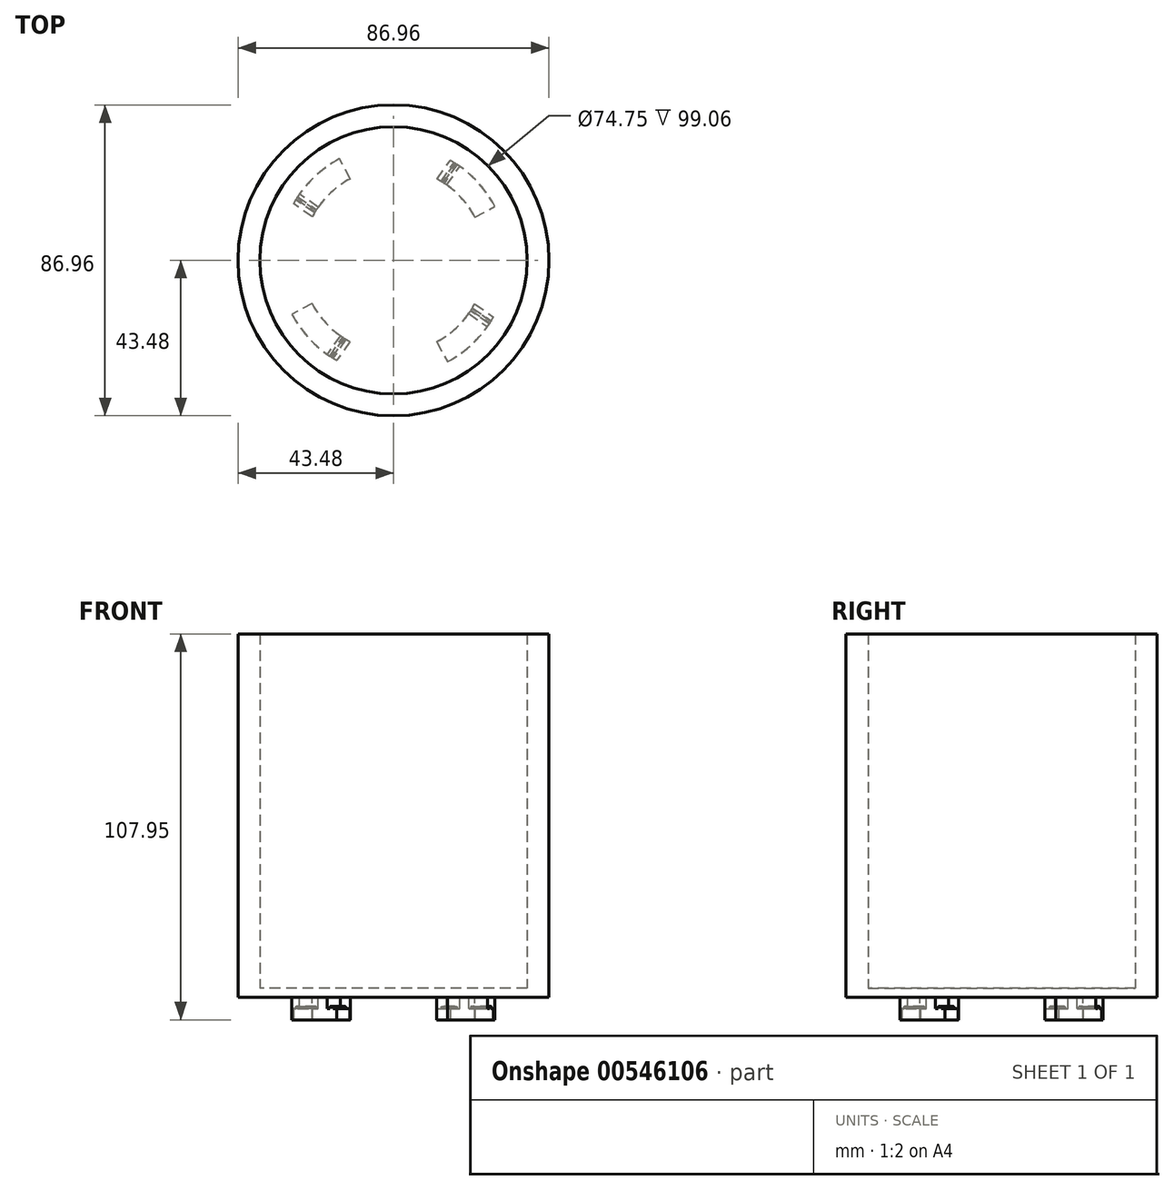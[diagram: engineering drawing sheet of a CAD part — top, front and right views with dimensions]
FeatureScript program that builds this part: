
annotation { "Feature Type Name" : "Feature", "Feature Type Description" : "" }
export const myFeature = defineFeature(function(context is Context, id is Id, definition is map)
    precondition{}
    {
        {
            var Q0;
            Q0=qCreatedBy(makeId("Top.planeOp"),FACE);
            var sketch = newSketch(context, id + "F0", { "sketchPlane" : qUnion([Q0])});
            skCircle(sketch, "E0", {"center": v(0, 0) * mm, "radius": 37.37 * mm});
            skCircle(sketch, "E1", {"center": v(0, 0) * mm, "radius": 43.48 * mm});
            skSolve(sketch);
        }
        {
            var Q0;
            Q0 = qSketchRegion(id + "F0", true);
            extrude(context, id + "F1", {"entities" : qUnion([Q0]), "depth" : 101.6 * mm, "offsetDistance" : 25.4 * mm});
        }
        {
            var Q0;
            Q0=qCreatedBy(makeId("Top.planeOp"),FACE);
            var sketch = newSketch(context, id + "F2", { "sketchPlane" : qUnion([Q0])});
            skCircle(sketch, "E2", {"center": v(0, 0) * mm, "radius": 43.48 * mm});
            skSolve(sketch);
        }
        {
            var Q0;
            Q0 = qSketchRegion(id + "F2", true);
            extrude(context, id + "F3", {"entities" : qUnion([Q0]), "operationType" : NewBodyOperationType.ADD, "depth" : 2.54 * mm, "offsetDistance" : 25.4 * mm});
        }
        {
            var Q0;
            Q0=makeQuery(id+"F3.boolean.opBoolean","MERGE",FACE,{"derivedFrom":[makeQuery(id+"F1.opExtrude","CAP_FACE",FACE,{"disambiguationData":[OSD([sQuery(id+"F0.wireOp",EDGE,"E0"),sQuery(id+"F0.wireOp",EDGE,"E1")])],"isStart":true}),makeQuery(id+"F3.opExtrude","CAP_FACE",FACE,{"disambiguationData":[OSD([sQuery(id+"F2.wireOp",EDGE,"E2")])],"isStart":true})]});
            var sketch = newSketch(context, id + "F4", { "sketchPlane" : qUnion([Q0])});
            skArc(sketch, "E3", {"start": v(15.08, 28.39) * mm, "mid": v(21.25, 24.12) * mm, "end": v(26.26, 18.53) * mm});
            skArc(sketch, "E4.0", {"start": v(12.1, 22.78) * mm, "mid": v(17.05, 19.35) * mm, "end": v(21.08, 14.87) * mm});
            skLineSegment(sketch, "E5", {"start": v(21.08, 14.87) * mm, "end": v(26.26, 18.53) * mm});
            skLineSegment(sketch, "E6", {"start": v(12.1, 22.78) * mm, "end": v(15.08, 28.39) * mm});
            skArc(sketch, "E7.1.0", {"start": v(-22.78, 12.1) * mm, "mid": v(-19.35, 17.05) * mm, "end": v(-14.87, 21.08) * mm});
            skLineSegment(sketch, "E7.1.1", {"start": v(-22.78, 12.1) * mm, "end": v(-28.39, 15.08) * mm});
            skArc(sketch, "E7.1.2", {"start": v(-28.39, 15.08) * mm, "mid": v(-24.12, 21.25) * mm, "end": v(-18.53, 26.26) * mm});
            skLineSegment(sketch, "E7.1.3", {"start": v(-14.87, 21.08) * mm, "end": v(-18.53, 26.26) * mm});
            skArc(sketch, "E7.2.0", {"start": v(-12.1, -22.78) * mm, "mid": v(-17.05, -19.35) * mm, "end": v(-21.08, -14.87) * mm});
            skLineSegment(sketch, "E7.2.1", {"start": v(-12.1, -22.78) * mm, "end": v(-15.08, -28.39) * mm});
            skArc(sketch, "E7.2.2", {"start": v(-15.08, -28.39) * mm, "mid": v(-21.25, -24.12) * mm, "end": v(-26.26, -18.53) * mm});
            skLineSegment(sketch, "E7.2.3", {"start": v(-21.08, -14.87) * mm, "end": v(-26.26, -18.53) * mm});
            skArc(sketch, "E7.3.0", {"start": v(22.78, -12.1) * mm, "mid": v(19.35, -17.05) * mm, "end": v(14.87, -21.08) * mm});
            skLineSegment(sketch, "E7.3.1", {"start": v(22.78, -12.1) * mm, "end": v(28.39, -15.08) * mm});
            skArc(sketch, "E7.3.2", {"start": v(28.39, -15.08) * mm, "mid": v(24.12, -21.25) * mm, "end": v(18.53, -26.26) * mm});
            skLineSegment(sketch, "E7.3.3", {"start": v(14.87, -21.08) * mm, "end": v(18.53, -26.26) * mm});
            skSolve(sketch);
        }
        {
            var Q0;
            Q0 = qSketchRegion(id + "F4", true);
            extrude(context, id + "F5", {"entities" : qUnion([Q0]), "operationType" : NewBodyOperationType.ADD, "depth" : 6.35 * mm, "offsetDistance" : 25.4 * mm});
        }
        {
            var Q0;
            Q0=makeQuery(id+"F5.opExtrude","CAP_FACE",FACE,{"disambiguationData":[OSD([sQuery(id+"F4.wireOp",EDGE,"E3"),sQuery(id+"F4.wireOp",EDGE,"E4.0"),sQuery(id+"F4.wireOp",EDGE,"E5"),sQuery(id+"F4.wireOp",EDGE,"E6")])],"isStart":false});
            var sketch = newSketch(context, id + "F6", { "sketchPlane" : qUnion([Q0])});
            skLineSegment(sketch, "E8.0", {"start": v(12.1, 22.78) * mm, "end": v(15.08, 28.39) * mm});
            skArc(sketch, "E8.1", {"start": v(15.08, 28.39) * mm, "mid": v(22.42, 23.04) * mm, "end": v(27.97, 15.84) * mm});
            skArc(sketch, "E8.2", {"start": v(12.1, 22.78) * mm, "mid": v(18.21, 18.26) * mm, "end": v(22.75, 12.16) * mm});
            skPoint(sketch, "E9.orphan", {"position": v(26.26, 18.53) * mm});
            skPoint(sketch, "E10.orphan", {"position": v(21.08, 14.87) * mm});
            skLineSegment(sketch, "E11", {"start": v(22.75, 12.16) * mm, "end": v(27.97, 15.84) * mm});
            skLineSegment(sketch, "E12.1.0", {"start": v(-22.78, 12.1) * mm, "end": v(-28.39, 15.08) * mm});
            skArc(sketch, "E12.1.1", {"start": v(-28.39, 15.08) * mm, "mid": v(-23.04, 22.42) * mm, "end": v(-15.84, 27.97) * mm});
            skArc(sketch, "E12.1.2", {"start": v(-22.78, 12.1) * mm, "mid": v(-18.26, 18.21) * mm, "end": v(-12.16, 22.75) * mm});
            skLineSegment(sketch, "E12.1.3", {"start": v(-12.16, 22.75) * mm, "end": v(-15.84, 27.97) * mm});
            skLineSegment(sketch, "E12.2.0", {"start": v(-12.1, -22.78) * mm, "end": v(-15.08, -28.39) * mm});
            skArc(sketch, "E12.2.1", {"start": v(-15.08, -28.39) * mm, "mid": v(-22.42, -23.04) * mm, "end": v(-27.97, -15.84) * mm});
            skArc(sketch, "E12.2.2", {"start": v(-12.1, -22.78) * mm, "mid": v(-18.21, -18.26) * mm, "end": v(-22.75, -12.16) * mm});
            skLineSegment(sketch, "E12.2.3", {"start": v(-22.75, -12.16) * mm, "end": v(-27.97, -15.84) * mm});
            skLineSegment(sketch, "E12.3.0", {"start": v(22.78, -12.1) * mm, "end": v(28.39, -15.08) * mm});
            skArc(sketch, "E12.3.1", {"start": v(28.39, -15.08) * mm, "mid": v(23.04, -22.42) * mm, "end": v(15.84, -27.97) * mm});
            skArc(sketch, "E12.3.2", {"start": v(22.78, -12.1) * mm, "mid": v(18.26, -18.21) * mm, "end": v(12.16, -22.75) * mm});
            skLineSegment(sketch, "E12.3.3", {"start": v(12.16, -22.75) * mm, "end": v(15.84, -27.97) * mm});
            skSolve(sketch);
        }
        {
            var Q0;
            Q0 = qSketchRegion(id + "F6", true);
            extrude(context, id + "F7", {"entities" : qUnion([Q0]), "operationType" : NewBodyOperationType.ADD, "oppositeDirection" : true, "depth" : 3.17 * mm, "offsetDistance" : 25.4 * mm});
        }
        {
            var Q0;
            Q0=makeQuery(id+"F7.opExtrude","CAP_FACE",FACE,{"disambiguationData":[OSD([sQuery(id+"F6.wireOp",EDGE,"E12.3.0"),sQuery(id+"F6.wireOp",EDGE,"E12.3.1"),sQuery(id+"F6.wireOp",EDGE,"E12.3.2"),sQuery(id+"F6.wireOp",EDGE,"E12.3.3")])],"isStart":false});
            var sketch = newSketch(context, id + "F8", { "sketchPlane" : qUnion([Q0])});
            skLineSegment(sketch, "E13", {"start": v(17.75, 26.8) * mm, "end": v(14.19, 21.54) * mm});
            skLineSegment(sketch, "E14", {"start": v(13.33, 22.08) * mm, "end": v(16.9, 27.34) * mm});
            skArc(sketch, "E15.0", {"start": v(14.19, 21.54) * mm, "mid": v(13.76, 21.81) * mm, "end": v(13.33, 22.08) * mm});
            skPoint(sketch, "E16.orphan", {"position": v(14.87, 21.08) * mm});
            skPoint(sketch, "E17.orphan", {"position": v(12.16, 22.75) * mm});
            skArc(sketch, "E18.0", {"start": v(17.75, 26.8) * mm, "mid": v(17.33, 27.07) * mm, "end": v(16.9, 27.34) * mm});
            skPoint(sketch, "E19.orphan", {"position": v(18.53, 26.26) * mm});
            skPoint(sketch, "E20.orphan", {"position": v(15.84, 27.97) * mm});
            skLineSegment(sketch, "E21.1.0", {"start": v(-26.8, 17.75) * mm, "end": v(-21.54, 14.19) * mm});
            skArc(sketch, "E21.1.1", {"start": v(-21.54, 14.19) * mm, "mid": v(-21.81, 13.76) * mm, "end": v(-22.08, 13.33) * mm});
            skArc(sketch, "E21.1.2", {"start": v(-26.8, 17.75) * mm, "mid": v(-27.07, 17.33) * mm, "end": v(-27.34, 16.9) * mm});
            skLineSegment(sketch, "E21.1.3", {"start": v(-22.08, 13.33) * mm, "end": v(-27.34, 16.9) * mm});
            skLineSegment(sketch, "E21.2.0", {"start": v(-17.75, -26.8) * mm, "end": v(-14.19, -21.54) * mm});
            skArc(sketch, "E21.2.1", {"start": v(-14.19, -21.54) * mm, "mid": v(-13.76, -21.81) * mm, "end": v(-13.33, -22.08) * mm});
            skArc(sketch, "E21.2.2", {"start": v(-17.75, -26.8) * mm, "mid": v(-17.33, -27.07) * mm, "end": v(-16.9, -27.34) * mm});
            skLineSegment(sketch, "E21.2.3", {"start": v(-13.33, -22.08) * mm, "end": v(-16.9, -27.34) * mm});
            skLineSegment(sketch, "E21.3.0", {"start": v(26.8, -17.75) * mm, "end": v(21.54, -14.19) * mm});
            skArc(sketch, "E21.3.1", {"start": v(21.54, -14.19) * mm, "mid": v(21.81, -13.76) * mm, "end": v(22.08, -13.33) * mm});
            skArc(sketch, "E21.3.2", {"start": v(26.8, -17.75) * mm, "mid": v(27.07, -17.33) * mm, "end": v(27.34, -16.9) * mm});
            skLineSegment(sketch, "E21.3.3", {"start": v(22.08, -13.33) * mm, "end": v(27.34, -16.9) * mm});
            skSolve(sketch);
        }
        {
            var Q0;
            Q0 = qSketchRegion(id + "F8", true);
            extrude(context, id + "F9", {"entities" : qUnion([Q0]), "operationType" : NewBodyOperationType.ADD, "depth" : 0.64 * mm, "offsetDistance" : 25.4 * mm});
        }
        {
            var Q0;
            Q0=makeQuery(id+"F9.opExtrude","CAP_EDGE",EDGE,{"disambiguationData":[OSD([sQuery(id+"F8.wireOp",EDGE,"E14")])],"isStart":false});
            var Q1;
            Q1=makeQuery(id+"F9.opExtrude","CAP_EDGE",EDGE,{"disambiguationData":[OSD([sQuery(id+"F8.wireOp",EDGE,"E13")])],"isStart":false});
            var Q2;
            Q2=makeQuery(id+"F9.opExtrude","CAP_EDGE",EDGE,{"disambiguationData":[OSD([sQuery(id+"F8.wireOp",EDGE,"E21.3.0")])],"isStart":false});
            var Q3;
            Q3=makeQuery(id+"F9.opExtrude","CAP_EDGE",EDGE,{"disambiguationData":[OSD([sQuery(id+"F8.wireOp",EDGE,"E21.3.3")])],"isStart":false});
            var Q4;
            Q4=makeQuery(id+"F9.opExtrude","CAP_EDGE",EDGE,{"disambiguationData":[OSD([sQuery(id+"F8.wireOp",EDGE,"E21.2.0")])],"isStart":false});
            var Q5;
            Q5=makeQuery(id+"F9.opExtrude","CAP_EDGE",EDGE,{"disambiguationData":[OSD([sQuery(id+"F8.wireOp",EDGE,"E21.2.3")])],"isStart":false});
            var Q6;
            Q6=makeQuery(id+"F9.opExtrude","CAP_EDGE",EDGE,{"disambiguationData":[OSD([sQuery(id+"F8.wireOp",EDGE,"E21.1.3")])],"isStart":false});
            var Q7;
            Q7=makeQuery(id+"F9.opExtrude","CAP_EDGE",EDGE,{"disambiguationData":[OSD([sQuery(id+"F8.wireOp",EDGE,"E21.1.0")])],"isStart":false});
            chamfer(context, id + "F10", {"entities" : qUnion([Q0, Q1, Q2, Q3, Q4, Q5, Q6, Q7]), "width" : 0.25 * mm, "tangentPropagation" : true});
        }
    });
